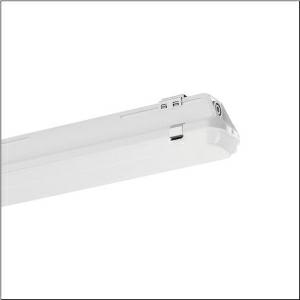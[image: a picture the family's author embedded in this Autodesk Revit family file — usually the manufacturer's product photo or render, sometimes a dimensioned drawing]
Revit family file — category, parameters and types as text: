
# Revit family: monsun_11_51fp10ep430l
name_source: partatom
category: Lighting Fixtures
units: mm (PartAtom-declared; Revit-internal decimal feet)

## family parameters
Cut with Voids When Loaded = No
Host = Face
Light Source = No
Part Type = Normal
Room Calculation Point = No
Round Connector Dimension = Use Diameter
Shared = No

## types (1)
- --- (1 x LED, 3840 lm, 20.5 W, 4000K)
    Apparent Load = 21 VA
    CIE Flux Codes = 47 77 93 94 100
    Color Rendering = 80
    Color Temperature = 4000K
    Default Elevation = 1800 mm
    Description = Monsun 11, damp-proof luminaire, chain hanger, primary optical cover: enclosure, of PMMA, light emission: direct distribution, primary light characteristic: symmetric, installation type: suspended mounting, surface-mounted, horizontal mounting, vertical mounting, LED, rated luminous flux: 3.840lm, luminous efficacy: 187lm/W, light colour: 840, colour temperature: 4000K, control gear: DALI 2, with terminal, 5-pole, max. 2.5mm², mains connection: 220..240V, AC, 50/60Hz, rated input power: 21W, luminaire housing, of glass-fibre reinforced polyester, uncoated, bright grey, incl. chain hanger, length: 1.590mm, width: 90mm, height: 88mm, clip for enclosure, of stainless steel (V2A), ceiling mounting element, of stainless steel (V2A), chain hanger, of stainless steel (V2A), protection rating (complete): IP66, insulation class (complete): insulation class I (protective earthing), certification: CE, ENEC, VDE, UKCA, protection symbol: D, impact resistance: IK04, permissible operating ambient temperature: -25..+40°C, standard: EN 50419, EN 60598-2-1, corresponds to IFS (International Featured Standards) requirements for safety and quality in the food industry, for indoor or canopied outdoor use, no direct snow, no direct sun, no direct rain, LABS conformity tested according to VDMA 24364:2018-05, contact your sales advisor before using the luminaires in applications with unclear chemical exposure, large temperature fluctuations or condensation-forming humidity, packaging unit: 1 piece
    Height = 89 mm
    Lamp = 1 x LED
    Lamp Light Flux = 3840 lm
    Lamp Power = 20.5 W
    Lamp count = 1
    Length = 1590 mm
    Luminous efficacy = 187 lm/W
    Manufacturer = Siteco
    ModVariant = No
    Model = 51FP10EP430L
    Mounting Place = Ceiling
    Mounting Type = Surface mounted
    Number of Poles = 1
    OnlyDefault = Yes
    Power Factor = 1
    Product Name = Monsun 11
    Product group = damp-proof luminaire
    ProductGroupID = 300
    Protection Class = Protection class I
    Protection Degree = IP 66
    RLX_Detail_Level = 1
    RLX_Emergency_Light_Flux = 0 lm
    RLX_Emergency_Type = 0
    RLX_Emergency_Type_DB = No
    RlxData = <blob elided: 91549 chars, md5=3e78127b>
    Socket = socket
    Standby Power = 0 W
    System Light Flux = 3840 lm
    System Power = 21 W
    Type Comments = factory setting: luminous flux: 100 % | dim-lin: 254 | 136 mA
    Type Image = l_1349237.jpg
    URL = http://relux.com
    VarID = @adj_033811
    Voltage = 0 V
    Weight = 0.00 kg
    Width = 90 mm

## geometry (parser evidence)
native form markers: Blend x4, Sweep x15
no freeform markers — native parametric forms only
